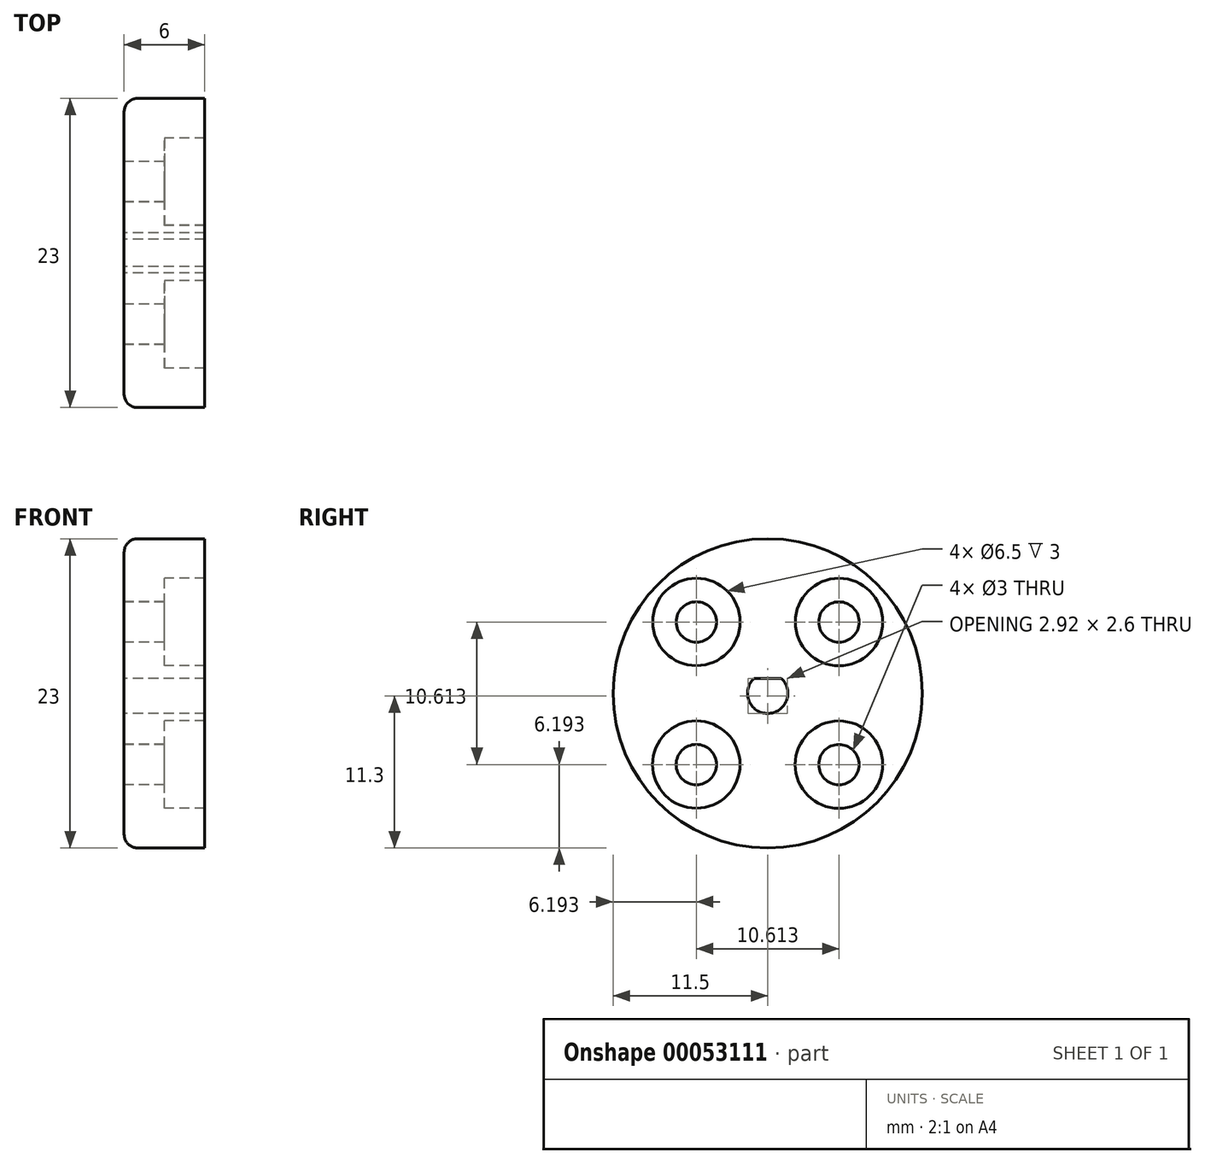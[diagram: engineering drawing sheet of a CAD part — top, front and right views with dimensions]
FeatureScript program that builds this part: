
annotation { "Feature Type Name" : "Feature", "Feature Type Description" : "" }
export const myFeature = defineFeature(function(context is Context, id is Id, definition is map)
    precondition{}
    {
        {
            var Q0;
            Q0=qCreatedBy(makeId("Right.planeOp"),FACE);
            var sketch = newSketch(context, id + "F0", { "sketchPlane" : qUnion([Q0])});
            skCircle(sketch, "E0", {"center": v(0, 0) * mm, "radius": 11.5 * mm});
            skCircle(sketch, "E1", {"center": v(5.3, 5.3) * mm, "radius": 3.25 * mm});
            skCircle(sketch, "E2", {"center": v(5.3, 5.3) * mm, "radius": 1.5 * mm});
            skCircle(sketch, "E3.1.0", {"center": v(-5.3, 5.3) * mm, "radius": 3.25 * mm});
            skCircle(sketch, "E3.1.1", {"center": v(-5.3, 5.3) * mm, "radius": 1.5 * mm});
            skCircle(sketch, "E3.2.0", {"center": v(-5.3, -5.3) * mm, "radius": 3.25 * mm});
            skCircle(sketch, "E3.2.1", {"center": v(-5.3, -5.3) * mm, "radius": 1.5 * mm});
            skCircle(sketch, "E3.3.0", {"center": v(5.3, -5.3) * mm, "radius": 3.25 * mm});
            skCircle(sketch, "E3.3.1", {"center": v(5.3, -5.3) * mm, "radius": 1.5 * mm});
            skCircle(sketch, "E4", {"center": v(0, 0) * mm, "radius": 1.5 * mm});
            skLineSegment(sketch, "E5", {"start": v(1.02, 1.1) * mm, "end": v(-1.02, 1.1) * mm});
            skSolve(sketch);
        }
        {
            var Q0;
            Q0=makeQuery(id+"F0.imprint","IMPRINT",FACE,{"disambiguationData":[TD([[makeQuery(id+"F0.imprint","IMPRINT",EDGE,{"derivedFrom":sQuery(id+"F0.wireOp",EDGE,"E0")}),1.0]])]});
            var Q1;
            {var subQ0=sQuery(id+"F0.wireOp",EDGE,"E5");Q1=makeQuery(id+"F0.imprint","IMPRINT",FACE,{"disambiguationData":[TD([[makeQuery(id+"F0.imprint","IMPRINT",EDGE,{"derivedFrom":subQ0}),-1.0]])]});}
            extrude(context, id + "F1", {"entities" : qUnion([Q0, Q1]), "depth" : 6 * mm});
        }
        {
            var Q0;
            Q0=makeQuery(id+"F0.imprint","IMPRINT",FACE,{"disambiguationData":[TD([[makeQuery(id+"F0.imprint","IMPRINT",EDGE,{"derivedFrom":sQuery(id+"F0.wireOp",EDGE,"E1")}),1.0]])]});
            var Q1;
            Q1=makeQuery(id+"F0.imprint","IMPRINT",FACE,{"disambiguationData":[TD([[makeQuery(id+"F0.imprint","IMPRINT",EDGE,{"derivedFrom":sQuery(id+"F0.wireOp",EDGE,"E3.2.0")}),1.0]])]});
            var Q2;
            Q2=makeQuery(id+"F0.imprint","IMPRINT",FACE,{"disambiguationData":[TD([[makeQuery(id+"F0.imprint","IMPRINT",EDGE,{"derivedFrom":sQuery(id+"F0.wireOp",EDGE,"E3.3.0")}),1.0]])]});
            var Q3;
            Q3=makeQuery(id+"F0.imprint","IMPRINT",FACE,{"disambiguationData":[TD([[makeQuery(id+"F0.imprint","IMPRINT",EDGE,{"derivedFrom":sQuery(id+"F0.wireOp",EDGE,"E3.1.0")}),1.0]])]});
            extrude(context, id + "F2", {"entities" : qUnion([Q0, Q1, Q2, Q3]), "operationType" : NewBodyOperationType.ADD, "depth" : 3 * mm});
        }
        {
            var Q0;
            Q0=makeQuery(id+"F1.opExtrude","CAP_EDGE",EDGE,{"disambiguationData":[OSD([sQuery(id+"F0.wireOp",EDGE,"E0")])],"isStart":true});
            fillet(context, id + "F3", {"entities" : qUnion([Q0]), "radius" : 1 * mm, "tangentPropagation" : true, "allowEdgeOverflow" : false});
        }
    });
